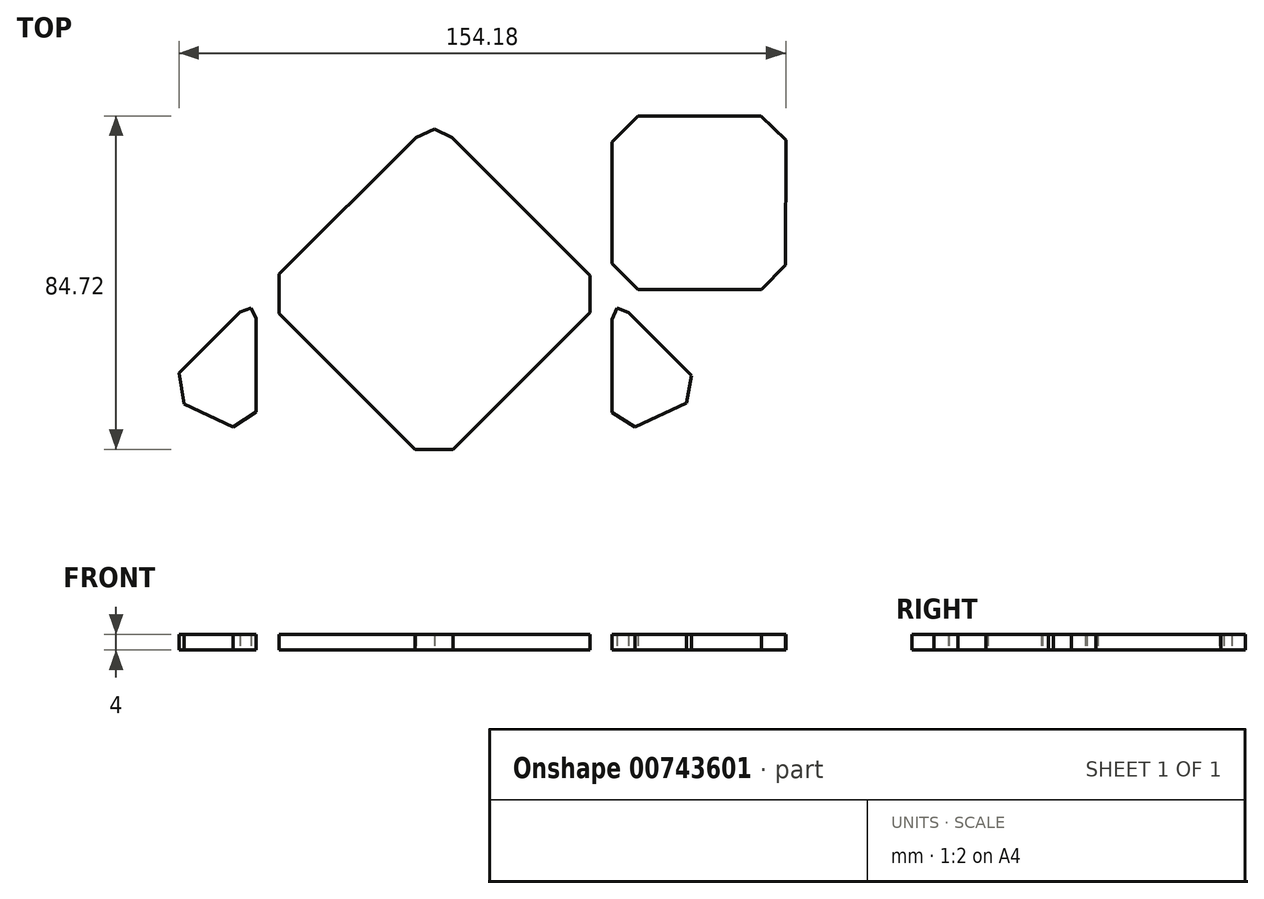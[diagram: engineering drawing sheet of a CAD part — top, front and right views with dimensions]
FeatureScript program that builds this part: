
annotation { "Feature Type Name" : "Feature", "Feature Type Description" : "" }
export const myFeature = defineFeature(function(context is Context, id is Id, definition is map)
    precondition{}
    {
        {
            var Q0;
            Q0=qCreatedBy(makeId("Top.planeOp"),FACE);
            var sketch = newSketch(context, id + "F0", { "sketchPlane" : qUnion([Q0])});
            skLineSegment(sketch, "E0", {"start": v(-12.16, 38.98) * mm, "end": v(-7.69, 36.89) * mm});
            skLineSegment(sketch, "E1", {"start": v(-7.69, 36.89) * mm, "end": v(6.52, 22.67) * mm});
            skLineSegment(sketch, "E2", {"start": v(6.52, 22.67) * mm, "end": v(27.4, 1.78) * mm});
            skLineSegment(sketch, "E3", {"start": v(27.4, 1.78) * mm, "end": v(27.35, -7.57) * mm});
            skLineSegment(sketch, "E4", {"start": v(27.35, -7.57) * mm, "end": v(-7.43, -42.36) * mm});
            skLineSegment(sketch, "E5", {"start": v(-7.43, -42.36) * mm, "end": v(-17.06, -42.36) * mm});
            skLineSegment(sketch, "E6", {"start": v(-17.06, -42.36) * mm, "end": v(-51.63, -7.87) * mm});
            skLineSegment(sketch, "E7", {"start": v(-51.63, -7.87) * mm, "end": v(-51.65, 2.14) * mm});
            skLineSegment(sketch, "E8", {"start": v(-51.65, 2.14) * mm, "end": v(-16.84, 36.9) * mm});
            skLineSegment(sketch, "E9", {"start": v(-16.84, 36.9) * mm, "end": v(-12.16, 38.98) * mm});
            skLineSegment(sketch, "E10", {"start": v(54.86, -1.76) * mm, "end": v(39.52, -1.76) * mm});
            skLineSegment(sketch, "E11", {"start": v(39.52, -1.76) * mm, "end": v(32.89, 4.87) * mm});
            skLineSegment(sketch, "E12", {"start": v(32.89, 4.87) * mm, "end": v(32.89, 35.72) * mm});
            skLineSegment(sketch, "E13", {"start": v(32.89, 35.72) * mm, "end": v(39.55, 42.31) * mm});
            skLineSegment(sketch, "E14", {"start": v(39.55, 42.31) * mm, "end": v(70.75, 42.36) * mm});
            skLineSegment(sketch, "E15", {"start": v(70.75, 42.36) * mm, "end": v(77.1, 36.16) * mm});
            skLineSegment(sketch, "E16", {"start": v(77.1, 36.16) * mm, "end": v(77.03, 4.43) * mm});
            skLineSegment(sketch, "E17", {"start": v(77.03, 4.43) * mm, "end": v(70.9, -1.75) * mm});
            skLineSegment(sketch, "E18", {"start": v(70.9, -1.75) * mm, "end": v(54.86, -1.76) * mm});
            skLineSegment(sketch, "E19", {"start": v(32.89, -21.23) * mm, "end": v(32.88, -10.67) * mm});
            skLineSegment(sketch, "E20", {"start": v(32.88, -10.67) * mm, "end": v(32.9, -9.44) * mm});
            skLineSegment(sketch, "E21", {"start": v(32.9, -9.44) * mm, "end": v(34.23, -6.4) * mm});
            skLineSegment(sketch, "E22", {"start": v(34.23, -6.4) * mm, "end": v(37.14, -7.63) * mm});
            skLineSegment(sketch, "E23", {"start": v(37.14, -7.63) * mm, "end": v(53.07, -23.57) * mm});
            skLineSegment(sketch, "E24", {"start": v(53.07, -23.57) * mm, "end": v(51.8, -30.6) * mm});
            skLineSegment(sketch, "E25", {"start": v(51.8, -30.6) * mm, "end": v(38.76, -36.74) * mm});
            skLineSegment(sketch, "E26", {"start": v(38.76, -36.74) * mm, "end": v(32.9, -33.03) * mm});
            skLineSegment(sketch, "E27", {"start": v(32.9, -33.03) * mm, "end": v(32.89, -21.23) * mm});
            skLineSegment(sketch, "E28", {"start": v(-57.5, -21.29) * mm, "end": v(-57.5, -32.91) * mm});
            skLineSegment(sketch, "E29", {"start": v(-57.5, -32.91) * mm, "end": v(-63.37, -36.72) * mm});
            skLineSegment(sketch, "E30", {"start": v(-63.37, -36.72) * mm, "end": v(-75.78, -30.89) * mm});
            skLineSegment(sketch, "E31", {"start": v(-75.78, -30.89) * mm, "end": v(-77.1, -23.02) * mm});
            skLineSegment(sketch, "E32", {"start": v(-77.1, -23.02) * mm, "end": v(-62.15, -8.08) * mm});
            skLineSegment(sketch, "E33", {"start": v(-62.15, -8.08) * mm, "end": v(-61.52, -7.46) * mm});
            skLineSegment(sketch, "E34", {"start": v(-61.52, -7.46) * mm, "end": v(-58.73, -6.42) * mm});
            skLineSegment(sketch, "E35", {"start": v(-58.73, -6.42) * mm, "end": v(-57.5, -9.14) * mm});
            skLineSegment(sketch, "E36", {"start": v(-57.5, -9.14) * mm, "end": v(-57.5, -21.29) * mm});
            skSolve(sketch);
        }
        {
            var Q0;
            Q0 = qSketchRegion(id + "F0", true);
            extrude(context, id + "F1", {"entities" : qUnion([Q0]), "depth" : 4 * mm, "offsetDistance" : 25 * mm});
        }
        {
            var Q0;
            Q0=qCreatedBy(makeId("Top.planeOp"),FACE);
            cPlane(context, id + "F2", {"entities" : qUnion([Q0]), "cplaneType" : CPlaneType.OFFSET, "offset" : 15 * mm, "oppositeDirection" : true, "width" : 150 * mm, "height" : 150 * mm});
        }
    });
